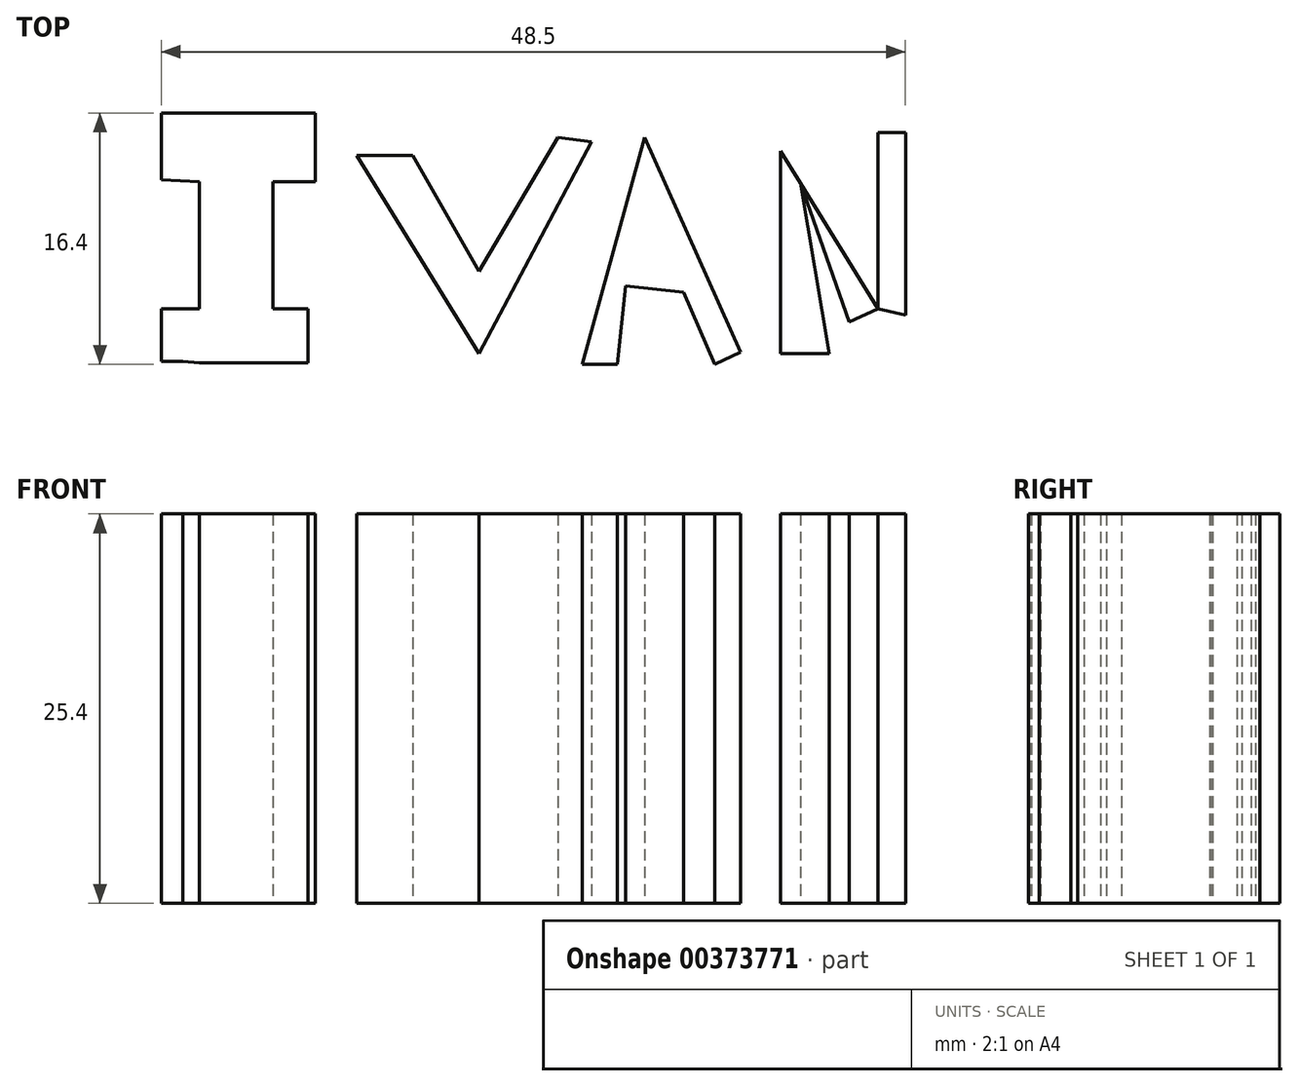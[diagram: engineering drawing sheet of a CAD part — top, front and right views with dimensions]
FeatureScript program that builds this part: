
annotation { "Feature Type Name" : "Feature", "Feature Type Description" : "" }
export const myFeature = defineFeature(function(context is Context, id is Id, definition is map)
    precondition{}
    {
        {
            var Q0;
            Q0=qCreatedBy(makeId("Top.planeOp"),FACE);
            var sketch = newSketch(context, id + "F0", { "sketchPlane" : qUnion([Q0])});
            skLineSegment(sketch, "E0", {"start": v(-18.2, 8.29) * mm, "end": v(-18.2, 0) * mm});
            skLineSegment(sketch, "E1", {"start": v(-18.2, 12.76) * mm, "end": v(-13.43, 12.76) * mm});
            skLineSegment(sketch, "E2", {"start": v(-10.65, 12.76) * mm, "end": v(-13.43, 12.76) * mm});
            skLineSegment(sketch, "E3", {"start": v(-10.65, 12.76) * mm, "end": v(-10.65, 8.29) * mm});
            skLineSegment(sketch, "E4", {"start": v(-10.65, 8.29) * mm, "end": v(-13.43, 8.29) * mm});
            skLineSegment(sketch, "E5", {"start": v(-13.43, 8.29) * mm, "end": v(-13.43, 0) * mm});
            skLineSegment(sketch, "E6", {"start": v(-13.43, -3.54) * mm, "end": v(-18.2, -3.54) * mm});
            skLineSegment(sketch, "E7", {"start": v(-18.2, 12.76) * mm, "end": v(-20.69, 12.76) * mm});
            skLineSegment(sketch, "E8", {"start": v(-20.69, 12.76) * mm, "end": v(-20.69, 8.39) * mm});
            skLineSegment(sketch, "E9", {"start": v(-20.69, 8.39) * mm, "end": v(-18.2, 8.29) * mm});
            skLineSegment(sketch, "E10", {"start": v(-18.2, 0) * mm, "end": v(-20.69, 0) * mm});
            skLineSegment(sketch, "E11", {"start": v(-20.69, 0) * mm, "end": v(-20.69, -3.44) * mm});
            skLineSegment(sketch, "E12", {"start": v(-20.69, -3.44) * mm, "end": v(-19.3, -3.44) * mm});
            skLineSegment(sketch, "E13", {"start": v(-19.3, -3.44) * mm, "end": v(-18.2, -3.54) * mm});
            skLineSegment(sketch, "E14", {"start": v(-13.43, 0) * mm, "end": v(-11.15, 0) * mm});
            skLineSegment(sketch, "E15", {"start": v(-11.15, 0) * mm, "end": v(-11.15, -3.54) * mm});
            skLineSegment(sketch, "E16", {"start": v(-11.15, -3.54) * mm, "end": v(-13.43, -3.54) * mm});
            skLineSegment(sketch, "E17", {"start": v(-7.97, 9.98) * mm, "end": v(0, -2.94) * mm});
            skLineSegment(sketch, "E18", {"start": v(7.34, 10.87) * mm, "end": v(0, -2.94) * mm});
            skLineSegment(sketch, "E19", {"start": v(-7.97, 9.98) * mm, "end": v(-4.29, 9.98) * mm});
            skLineSegment(sketch, "E20", {"start": v(-4.29, 9.98) * mm, "end": v(0, 2.43) * mm});
            skLineSegment(sketch, "E21", {"start": v(0, 2.43) * mm, "end": v(5.15, 11.17) * mm});
            skLineSegment(sketch, "E22", {"start": v(5.15, 11.17) * mm, "end": v(7.34, 10.87) * mm});
            skLineSegment(sketch, "E23", {"start": v(10.82, 11.17) * mm, "end": v(6.74, -3.64) * mm});
            skLineSegment(sketch, "E24", {"start": v(6.74, -3.64) * mm, "end": v(10.82, 11.17) * mm});
            skLineSegment(sketch, "E25", {"start": v(10.82, 11.17) * mm, "end": v(17.08, -2.84) * mm});
            skLineSegment(sketch, "E26", {"start": v(8.78, 3.77) * mm, "end": v(14.12, 3.77) * mm});
            skLineSegment(sketch, "E27", {"start": v(6.74, -3.64) * mm, "end": v(9.03, -3.64) * mm});
            skLineSegment(sketch, "E28", {"start": v(9.03, -3.64) * mm, "end": v(9.57, 1.46) * mm});
            skLineSegment(sketch, "E29", {"start": v(9.57, 1.46) * mm, "end": v(13.34, 1.07) * mm});
            skLineSegment(sketch, "E30", {"start": v(13.34, 1.07) * mm, "end": v(15.39, -3.64) * mm});
            skLineSegment(sketch, "E31", {"start": v(15.39, -3.64) * mm, "end": v(17.08, -2.84) * mm});
            skLineSegment(sketch, "E32", {"start": v(9.4, 6.02) * mm, "end": v(13.12, 6.02) * mm});
            skLineSegment(sketch, "E33", {"start": v(19.66, 10.28) * mm, "end": v(19.66, -2.94) * mm});
            skLineSegment(sketch, "E34", {"start": v(19.66, 10.28) * mm, "end": v(26.02, 0) * mm});
            skLineSegment(sketch, "E35", {"start": v(26.02, 11.47) * mm, "end": v(26.02, 0) * mm});
            skLineSegment(sketch, "E36", {"start": v(19.66, -2.94) * mm, "end": v(22.84, -2.94) * mm});
            skLineSegment(sketch, "E37", {"start": v(22.84, -2.94) * mm, "end": v(20.96, 8.18) * mm});
            skLineSegment(sketch, "E38", {"start": v(20.96, 8.18) * mm, "end": v(24.13, -0.85) * mm});
            skLineSegment(sketch, "E39", {"start": v(24.13, -0.85) * mm, "end": v(26.02, 0) * mm});
            skLineSegment(sketch, "E40", {"start": v(26.02, 0) * mm, "end": v(27.81, -0.43) * mm});
            skPoint(sketch, "E40.endSnap0", {"position": v(25.08, -0.43) * mm});
            skLineSegment(sketch, "E41", {"start": v(27.81, -0.43) * mm, "end": v(27.81, 11.47) * mm});
            skLineSegment(sketch, "E42", {"start": v(27.81, 11.47) * mm, "end": v(26.02, 11.47) * mm});
            skSolve(sketch);
        }
        {
            var Q0;
            Q0=makeQuery(id+"F0.imprint","IMPRINT",FACE,{"disambiguationData":[TD([[makeQuery(id+"F0.imprint","IMPRINT",EDGE,{"derivedFrom":sQuery(id+"F0.wireOp",EDGE,"E17")}),1.0]])]});
            var Q1;
            {var subQ1=sQuery(id+"F0.wireOp",EDGE,"E26");Q1=makeQuery(id+"F0.imprint","IMPRINT",FACE,{"disambiguationData":[TD([[makeQuery(id+"F0.imprint","IMPRINT",EDGE,{"derivedFrom":subQ1}),-1.0]])]});}
            var Q2;
            Q2=makeQuery(id+"F0.imprint","IMPRINT",FACE,{"disambiguationData":[TD([[makeQuery(id+"F0.imprint","IMPRINT",EDGE,{"derivedFrom":sQuery(id+"F0.wireOp",EDGE,"E0")}),1.0]])]});
            var Q3;
            Q3=makeQuery(id+"F0.imprint","IMPRINT",FACE,{"disambiguationData":[TD([[makeQuery(id+"F0.imprint","IMPRINT",EDGE,{"derivedFrom":sQuery(id+"F0.wireOp",EDGE,"E35")}),1.0]])]});
            var Q4;
            {var subQ0=sQuery(id+"F0.wireOp",EDGE,"E33");Q4=makeQuery(id+"F0.imprint","IMPRINT",FACE,{"disambiguationData":[TD([[makeQuery(id+"F0.imprint","IMPRINT",EDGE,{"derivedFrom":subQ0}),1.0]])]});}
            var Q5;
            {var subQ2=sQuery(id+"F0.wireOp",EDGE,"E38");Q5=makeQuery(id+"F0.imprint","IMPRINT",FACE,{"disambiguationData":[TD([[makeQuery(id+"F0.imprint","IMPRINT",EDGE,{"derivedFrom":subQ2}),1.0]])]});}
            var Q6;
            {var subQ3=sQuery(id+"F0.wireOp",EDGE,"E32");Q6=makeQuery(id+"F0.imprint","IMPRINT",FACE,{"disambiguationData":[TD([[makeQuery(id+"F0.imprint","IMPRINT",EDGE,{"derivedFrom":subQ3}),1.0]])]});}
            var Q7;
            {var subQ0=sQuery(id+"F0.wireOp",EDGE,"E26");Q7=makeQuery(id+"F0.imprint","IMPRINT",FACE,{"disambiguationData":[TD([[makeQuery(id+"F0.imprint","IMPRINT",EDGE,{"derivedFrom":subQ0}),1.0]])]});}
            extrude(context, id + "F1", {"entities" : qUnion([Q0, Q1, Q2, Q3, Q4, Q5, Q6, Q7]), "depth" : 25.4 * mm});
        }
    });
